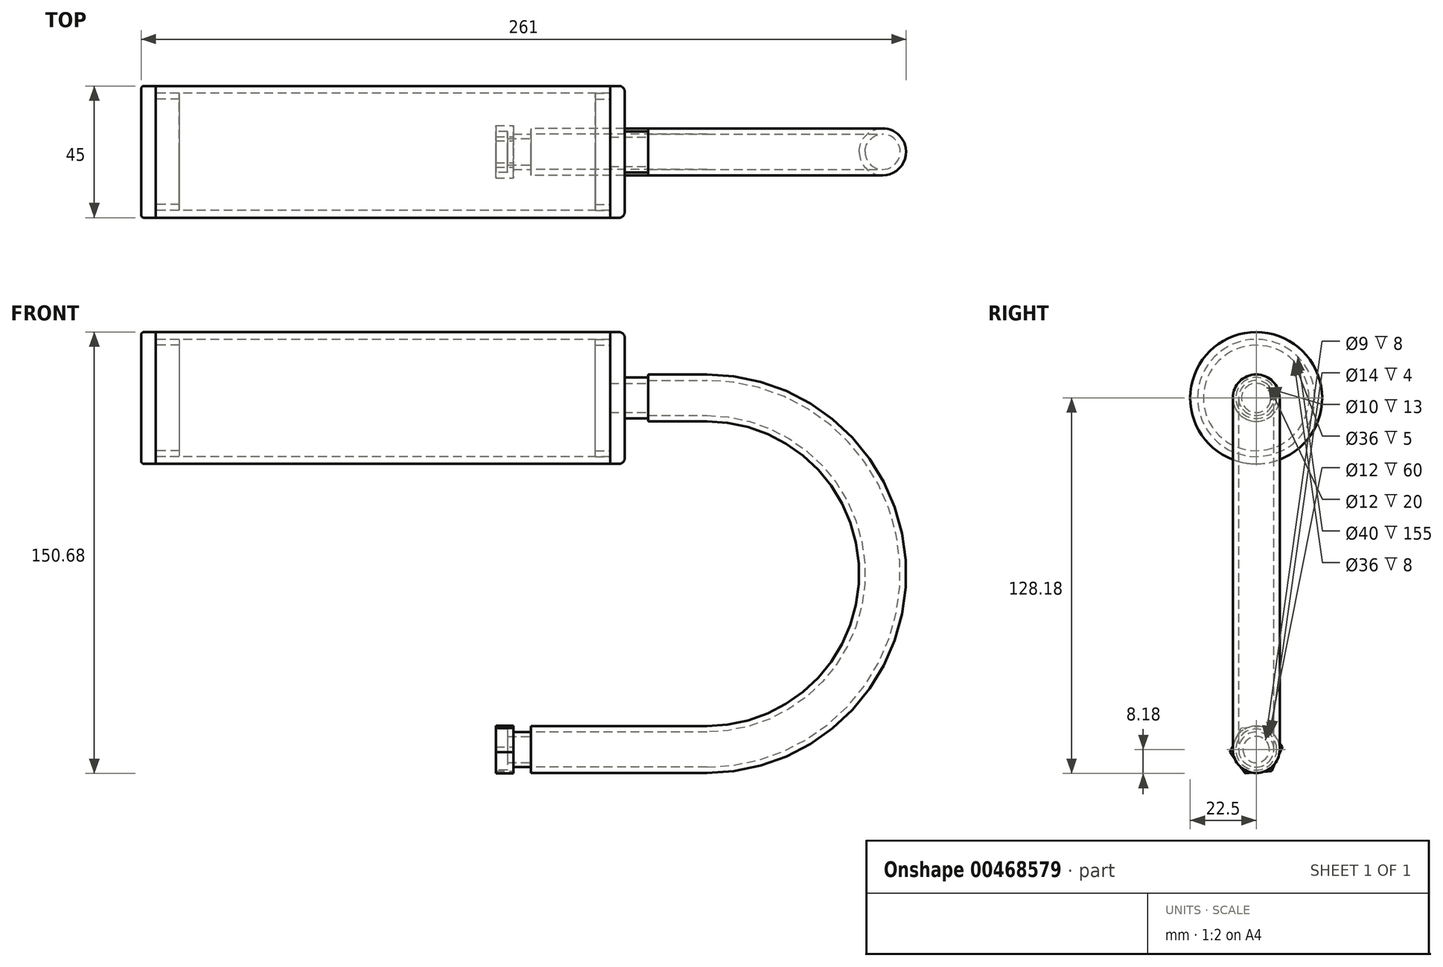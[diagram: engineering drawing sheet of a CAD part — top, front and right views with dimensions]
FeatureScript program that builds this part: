
annotation { "Feature Type Name" : "Feature", "Feature Type Description" : "" }
export const myFeature = defineFeature(function(context is Context, id is Id, definition is map)
    precondition{}
    {
        {
            var Q0;
            Q0=qCreatedBy(makeId("Front.planeOp"),FACE);
            var sketch = newSketch(context, id + "F0", { "sketchPlane" : qUnion([Q0])});
            skLineSegment(sketch, "E0", {"start": v(0, 0) * mm, "end": v(155, 0) * mm});
            skLineSegment(sketch, "E1", {"start": v(155, 0) * mm, "end": v(155, 22.5) * mm});
            skLineSegment(sketch, "E2", {"start": v(155, 22.5) * mm, "end": v(0, 22.5) * mm});
            skLineSegment(sketch, "E3", {"start": v(0, 22.5) * mm, "end": v(0, 0) * mm});
            skLineSegment(sketch, "E4", {"start": v(155, 20) * mm, "end": v(0, 20) * mm});
            skPoint(sketch, "E5", {"position": v(150, 20) * mm});
            skLineSegment(sketch, "E6", {"start": v(150, 20) * mm, "end": v(150, 18) * mm});
            skLineSegment(sketch, "E7", {"start": v(150, 18) * mm, "end": v(155, 18) * mm});
            skLineSegment(sketch, "E8", {"start": v(155, 22.5) * mm, "end": v(160, 22.5) * mm});
            skLineSegment(sketch, "E9", {"start": v(160, 22.5) * mm, "end": v(160, 0) * mm});
            skLineSegment(sketch, "E10", {"start": v(160, 0) * mm, "end": v(155, 0) * mm});
            skLineSegment(sketch, "E11", {"start": v(155, 5) * mm, "end": v(160, 5) * mm});
            skLineSegment(sketch, "E12", {"start": v(160, 5) * mm, "end": v(168, 5) * mm});
            skLineSegment(sketch, "E13", {"start": v(168, 5) * mm, "end": v(168, 0) * mm});
            skLineSegment(sketch, "E14", {"start": v(168, 0) * mm, "end": v(160, 0) * mm});
            skLineSegment(sketch, "E15", {"start": v(168, 5) * mm, "end": v(168, 7) * mm});
            skLineSegment(sketch, "E16", {"start": v(168, 7) * mm, "end": v(160, 7) * mm});
            skSolve(sketch);
        }
        {
            var Q0;
            {var subQ0=sQuery(id+"F0.wireOp",EDGE,"E2");Q0=makeQuery(id+"F0.imprint","IMPRINT",FACE,{"disambiguationData":[TD([[makeQuery(id+"F0.imprint","IMPRINT",EDGE,{"derivedFrom":subQ0}),1.0]])]});}
            var Q1;
            Q1=sQuery(id+"F0.wireOp",EDGE,"E0");
            revolve(context, id + "F1", {"surfaceOperationType" : NewSurfaceOperationType.NEW, "entities" : qUnion([Q0]), "axis" : qUnion([Q1]), "revolveType" : RevolveType.FULL});
        }
        {
            var Q0;
            {var subQ0=sQuery(id+"F0.wireOp",EDGE,"E8");Q0=makeQuery(id+"F0.imprint","IMPRINT",FACE,{"disambiguationData":[TD([[makeQuery(id+"F0.imprint","IMPRINT",EDGE,{"derivedFrom":subQ0}),-1.0]])]});}
            var Q1;
            {var subQ0=sQuery(id+"F0.wireOp",EDGE,"E12");Q1=makeQuery(id+"F0.imprint","IMPRINT",FACE,{"disambiguationData":[TD([[makeQuery(id+"F0.imprint","IMPRINT",EDGE,{"derivedFrom":subQ0}),1.0]])]});}
            var Q2;
            {var subQ4=sQuery(id+"F0.wireOp",EDGE,"E6");Q2=makeQuery(id+"F0.imprint","IMPRINT",FACE,{"disambiguationData":[TD([[makeQuery(id+"F0.imprint","IMPRINT",EDGE,{"derivedFrom":subQ4}),1.0]])]});}
            var Q3;
            Q3=sQuery(id+"F0.wireOp",EDGE,"E14");
            revolve(context, id + "F2", {"surfaceOperationType" : NewSurfaceOperationType.NEW, "entities" : qUnion([Q0, Q1, Q2]), "axis" : qUnion([Q3]), "revolveType" : RevolveType.FULL});
        }
        {
            var Q0;
            Q0=makeQuery(id+"F2.opRevolve","SWEPT_EDGE",EDGE,{"disambiguationData":[OSD([sQuery(id+"F0.wireOp",EDGE,"E8"),sQuery(id+"F0.wireOp",EDGE,"E9")])]});
            fillet(context, id + "F3", {"entities" : qUnion([Q0]), "radius" : 2 * mm, "tangentPropagation" : true, "allowEdgeOverflow" : false});
        }
        {
            var Q0;
            Q0=qCreatedBy(makeId("Front.planeOp"),FACE);
            var sketch = newSketch(context, id + "F4", { "sketchPlane" : qUnion([Q0])});
            skLineSegment(sketch, "E17.0", {"start": v(168, 5) * mm, "end": v(168, -5) * mm});
            skPoint(sketch, "E18", {"position": v(188, 0) * mm});
            skPoint(sketch, "E18.positionSnap0", {"position": v(168, 0) * mm});
            skPoint(sketch, "E19", {"position": v(248, -60) * mm});
            skPoint(sketch, "E20", {"position": v(188, -120) * mm});
            skLineSegment(sketch, "E21", {"start": v(168, 0) * mm, "end": v(188, 0) * mm});
            skArc(sketch, "E22", {"start": v(188, -120) * mm, "mid": v(248, -60) * mm, "end": v(188, 0) * mm});
            skLineSegment(sketch, "E23", {"start": v(188, -120) * mm, "end": v(128, -120) * mm});
            skSolve(sketch);
        }
        {
            var Q0;
            Q0=makeQuery(id+"F2.opRevolve","SWEPT_FACE",FACE,{"disambiguationData":[OSD([sQuery(id+"F0.wireOp",EDGE,"E15")])]});
            var sketch = newSketch(context, id + "F5", { "sketchPlane" : qUnion([Q0])});
            skCircle(sketch, "E24", {"center": v(0, 0) * mm, "radius": 8 * mm});
            skCircle(sketch, "E25", {"center": v(0, 0) * mm, "radius": 6 * mm});
            skSolve(sketch);
        }
        {
            var Q0;
            Q0=qCreatedBy(makeId("Front.planeOp"),FACE);
            var sketch = newSketch(context, id + "F6", { "sketchPlane" : qUnion([Q0])});
            skLineSegment(sketch, "E26.0", {"start": v(0, -20) * mm, "end": v(0, 20) * mm});
            skLineSegment(sketch, "E27", {"start": v(0, 20) * mm, "end": v(8, 20) * mm});
            skLineSegment(sketch, "E28", {"start": v(8, 20) * mm, "end": v(8, 18) * mm});
            skLineSegment(sketch, "E29", {"start": v(8, 18) * mm, "end": v(-5, 18) * mm});
            skLineSegment(sketch, "E30", {"start": v(0, 20) * mm, "end": v(0, 22.5) * mm});
            skLineSegment(sketch, "E31", {"start": v(0, 22.5) * mm, "end": v(-5, 22.5) * mm});
            skLineSegment(sketch, "E32", {"start": v(-5, 22.5) * mm, "end": v(-5, 0) * mm});
            skLineSegment(sketch, "E33", {"start": v(-5, 0) * mm, "end": v(0, 0) * mm});
            skLineSegment(sketch, "E34", {"start": v(0, 0) * mm, "end": v(0, 20) * mm});
            skSolve(sketch);
        }
        {
            var Q0;
            Q0 = qSketchRegion(id + "F6", true);
            var Q1;
            Q1=sQuery(id+"F6.wireOp",EDGE,"E33");
            revolve(context, id + "F7", {"surfaceOperationType" : NewSurfaceOperationType.NEW, "entities" : qUnion([Q0]), "axis" : qUnion([Q1]), "revolveType" : RevolveType.FULL});
        }
        {
            var Q0;
            Q0=makeQuery(id+"F7.opRevolve","SWEPT_EDGE",EDGE,{"disambiguationData":[OSD([sQuery(id+"F6.wireOp",EDGE,"E31"),sQuery(id+"F6.wireOp",EDGE,"E32")])]});
            fillet(context, id + "F8", {"entities" : qUnion([Q0]), "radius" : 1 * mm, "tangentPropagation" : true, "allowEdgeOverflow" : false});
        }
        {
            var Q0;
            Q0 = qSketchRegion(id + "F5", true);
            var Q1;
            Q1=sQuery(id+"F4.wireOp",EDGE,"E21");
            var Q2;
            Q2=sQuery(id+"F4.wireOp",EDGE,"E22");
            var Q3;
            Q3=sQuery(id+"F4.wireOp",EDGE,"E23");
            sweep(context, id + "F9", {"profiles" : qUnion([Q0]), "path" : qUnion([Q1, Q2, Q3])});
        }
        {
            var Q0;
            Q0=makeQuery(id+"F9.opSweep","CAP_FACE",FACE,{"disambiguationData":[OSD([sQuery(id+"F4.wireOp",VERTEX,"E23.end"),sQuery(id+"F5.wireOp",EDGE,"2d8d58ff-2043-493c-a378-837521a0f7ff.0"),sQuery(id+"F5.wireOp",EDGE,"E24")])],"isStart":false});
            var sketch = newSketch(context, id + "F10", { "sketchPlane" : qUnion([Q0])});
            skCircle(sketch, "E35.0", {"center": v(0, -120) * mm, "radius": 6 * mm});
            skCircle(sketch, "E36", {"center": v(0, -120) * mm, "radius": 4.5 * mm});
            skSolve(sketch);
        }
        {
            var Q0;
            Q0 = qSketchRegion(id + "F10", true);
            extrude(context, id + "F11", {"entities" : qUnion([Q0]), "depth" : 8 * mm, "offsetDistance" : 25 * mm});
        }
        {
            var Q0;
            Q0=makeQuery(id+"F11.opExtrude","CAP_FACE",FACE,{"disambiguationData":[OSD([sQuery(id+"F10.wireOp",EDGE,"E35.0"),sQuery(id+"F10.wireOp",EDGE,"E36")])],"isStart":false});
            cPlane(context, id + "F12", {"entities" : qUnion([Q0]), "cplaneType" : CPlaneType.OFFSET, "offset" : 2 * mm, "oppositeDirection" : true, "width" : 150 * mm, "height" : 150 * mm});
        }
        {
            var Q0;
            Q0=qCreatedBy(id+"F12.planeOp",FACE);
            var sketch = newSketch(context, id + "F13", { "sketchPlane" : qUnion([Q0])});
            skCircle(sketch, "E37.0", {"center": v(0, -120) * mm, "radius": 6 * mm});
            skCircle(sketch, "E38", {"center": v(0, -120) * mm, "radius": 9 * mm});
            skSolve(sketch);
        }
        {
            var Q0;
            Q0 = qSketchRegion(id + "F13", true);
            extrude(context, id + "F14", {"entities" : qUnion([Q0]), "operationType" : NewBodyOperationType.ADD, "depth" : 6 * mm, "offsetDistance" : 25 * mm});
        }
        {
            var Q0;
            Q0=makeQuery(id+"F14.opExtrude","CAP_FACE",FACE,{"disambiguationData":[OSD([sQuery(id+"F13.wireOp",EDGE,"E37.0"),sQuery(id+"F13.wireOp",EDGE,"E38")])],"isStart":false});
            var sketch = newSketch(context, id + "F15", { "sketchPlane" : qUnion([Q0])});
            skCircle(sketch, "E39.0", {"center": v(0, -120) * mm, "radius": 6 * mm});
            skCircle(sketch, "E40", {"center": v(0, -120) * mm, "radius": 7 * mm});
            skSolve(sketch);
        }
        {
            var Q0;
            Q0 = qSketchRegion(id + "F15", true);
            extrude(context, id + "F16", {"entities" : qUnion([Q0]), "operationType" : NewBodyOperationType.REMOVE, "oppositeDirection" : true, "depth" : 4 * mm, "offsetDistance" : 25 * mm});
        }
        {
            var Q0;
            Q0=makeQuery(id+"F14.opExtrude","CAP_FACE",FACE,{"disambiguationData":[OSD([sQuery(id+"F13.wireOp",EDGE,"E37.0"),sQuery(id+"F13.wireOp",EDGE,"E38")])],"isStart":true});
            var sketch = newSketch(context, id + "F17", { "sketchPlane" : qUnion([Q0])});
            skCircle(sketch, "E41.0", {"center": v(0, -120) * mm, "radius": 6 * mm, "construction": true});
            skCircle(sketch, "E42.cCircle", {"center": v(0, -120) * mm, "radius": 7.8 * mm, "construction": true});
            skLineSegment(sketch, "E42.0", {"start": v(-8.96, -120.83) * mm, "end": v(-5.2, -112.66) * mm});
            skLineSegment(sketch, "E42.1", {"start": v(-5.2, -112.66) * mm, "end": v(3.76, -111.82) * mm});
            skLineSegment(sketch, "E42.2", {"start": v(3.76, -111.82) * mm, "end": v(8.96, -119.17) * mm});
            skLineSegment(sketch, "E42.3", {"start": v(8.96, -119.17) * mm, "end": v(5.2, -127.34) * mm});
            skLineSegment(sketch, "E42.4", {"start": v(5.2, -127.34) * mm, "end": v(-3.76, -128.18) * mm});
            skLineSegment(sketch, "E42.5", {"start": v(-3.76, -128.18) * mm, "end": v(-8.96, -120.83) * mm});
            skPoint(sketch, "E42.0.midPoint", {"position": v(-7.08, -116.74) * mm});
            skCircle(sketch, "E43.0", {"center": v(0, -120) * mm, "radius": 9 * mm});
            skSolve(sketch);
        }
        {
            var Q0;
            {var subQ0=sQuery(id+"F17.wireOp",EDGE,"E42.4");Q0=makeQuery(id+"F17.imprint","IMPRINT",FACE,{"disambiguationData":[TD([[makeQuery(id+"F17.imprint","IMPRINT",EDGE,{"derivedFrom":subQ0}),1.0]])]});}
            var Q1;
            {var subQ0=sQuery(id+"F17.wireOp",EDGE,"E42.3");Q1=makeQuery(id+"F17.imprint","IMPRINT",FACE,{"disambiguationData":[TD([[makeQuery(id+"F17.imprint","IMPRINT",EDGE,{"derivedFrom":subQ0}),1.0]])]});}
            var Q2;
            {var subQ0=sQuery(id+"F17.wireOp",EDGE,"E42.2");Q2=makeQuery(id+"F17.imprint","IMPRINT",FACE,{"disambiguationData":[TD([[makeQuery(id+"F17.imprint","IMPRINT",EDGE,{"derivedFrom":subQ0}),1.0]])]});}
            var Q3;
            {var subQ0=sQuery(id+"F17.wireOp",EDGE,"E42.1");Q3=makeQuery(id+"F17.imprint","IMPRINT",FACE,{"disambiguationData":[TD([[makeQuery(id+"F17.imprint","IMPRINT",EDGE,{"derivedFrom":subQ0}),1.0]])]});}
            var Q4;
            {var subQ0=sQuery(id+"F17.wireOp",EDGE,"E42.0");Q4=makeQuery(id+"F17.imprint","IMPRINT",FACE,{"disambiguationData":[TD([[makeQuery(id+"F17.imprint","IMPRINT",EDGE,{"derivedFrom":subQ0}),1.0]])]});}
            var Q5;
            {var subQ0=sQuery(id+"F17.wireOp",EDGE,"E42.5");Q5=makeQuery(id+"F17.imprint","IMPRINT",FACE,{"disambiguationData":[TD([[makeQuery(id+"F17.imprint","IMPRINT",EDGE,{"derivedFrom":subQ0}),1.0]])]});}
            extrude(context, id + "F18", {"entities" : qUnion([Q0, Q1, Q2, Q3, Q4, Q5]), "operationType" : NewBodyOperationType.REMOVE, "oppositeDirection" : true, "depth" : 6 * mm, "offsetDistance" : 25 * mm});
        }
    });
